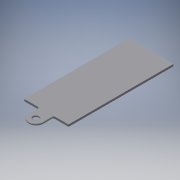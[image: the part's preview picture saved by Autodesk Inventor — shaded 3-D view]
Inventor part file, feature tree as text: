
AUTODESK INVENTOR PART (.ipt)
format: ipt  version: 2019 (Build 230136000, 136)  size: 191,488 bytes
history: native  units: mm
features: sketch x7, extrude x6, fillet x2, projected_geometry x2, hole x1
ambient origin geometry x8: Origin, YZ Plane, XZ Plane, XY Plane, X Axis, Y Axis, Z Axis, Center Point
bodies: Solid1 (feature_tree)
feature tree (18):
  extrude  "Extrusion1"  Depth=40.0mm
  extrude  "Extrusion2"  TaperAngle=0.0deg  [1 undecoded]
  extrude  "Extrusion4"  Depth=2.0mm
  hole  "Hole1"  [1 undecoded]
  extrude  "Extrusion6"  Depth=2.0mm
  fillet  "Fillet1"  [1 undecoded]
  fillet  "Fillet2"  [1 undecoded]
  extrude  "Extrusion7"  TaperAngle=0.0deg  [1 undecoded]
  extrude  "Extrusion8"  Depth=1.0mm
  sketch  "Sketch1"  dims[d1=100.0mm d2=40.0mm]
  sketch  "Sketch2"  dims[d3=4.0mm d4=0.0mm]
  projected_geometry  "Projected Loop1"
  sketch  "Sketch4"  dims[d5=2.0mm d6=2.0mm]
  sketch  "Sketch5"  dims[d7=0.0mm d12=15.0mm]
  sketch  "Sketch8"  dims[d13=10.0mm d14=2.0mm d15=0.0mm]
  sketch  "Sketch9"  dims[d16=5.5mm d17=6.0mm d18=9.4mm d19=2.0mm d20=90.0deg d21=8.0mm d22=20.594885mm d27=45.0deg]
  sketch  "Sketch10"  dims[d28=2.0mm d29=0.0mm d30=1.0mm d31=1.0mm d32=4.0mm d33=5.0mm d34=2.0mm d35=0.0mm d36=2.0mm d37=0.0mm]
  projected_geometry  "Projected Loop4"
note: 5 required parameter values undecoded (feature->parameter linkage not recoverable at this tier; creation-order binding heuristic only, values carry confidence <= 0.55)
